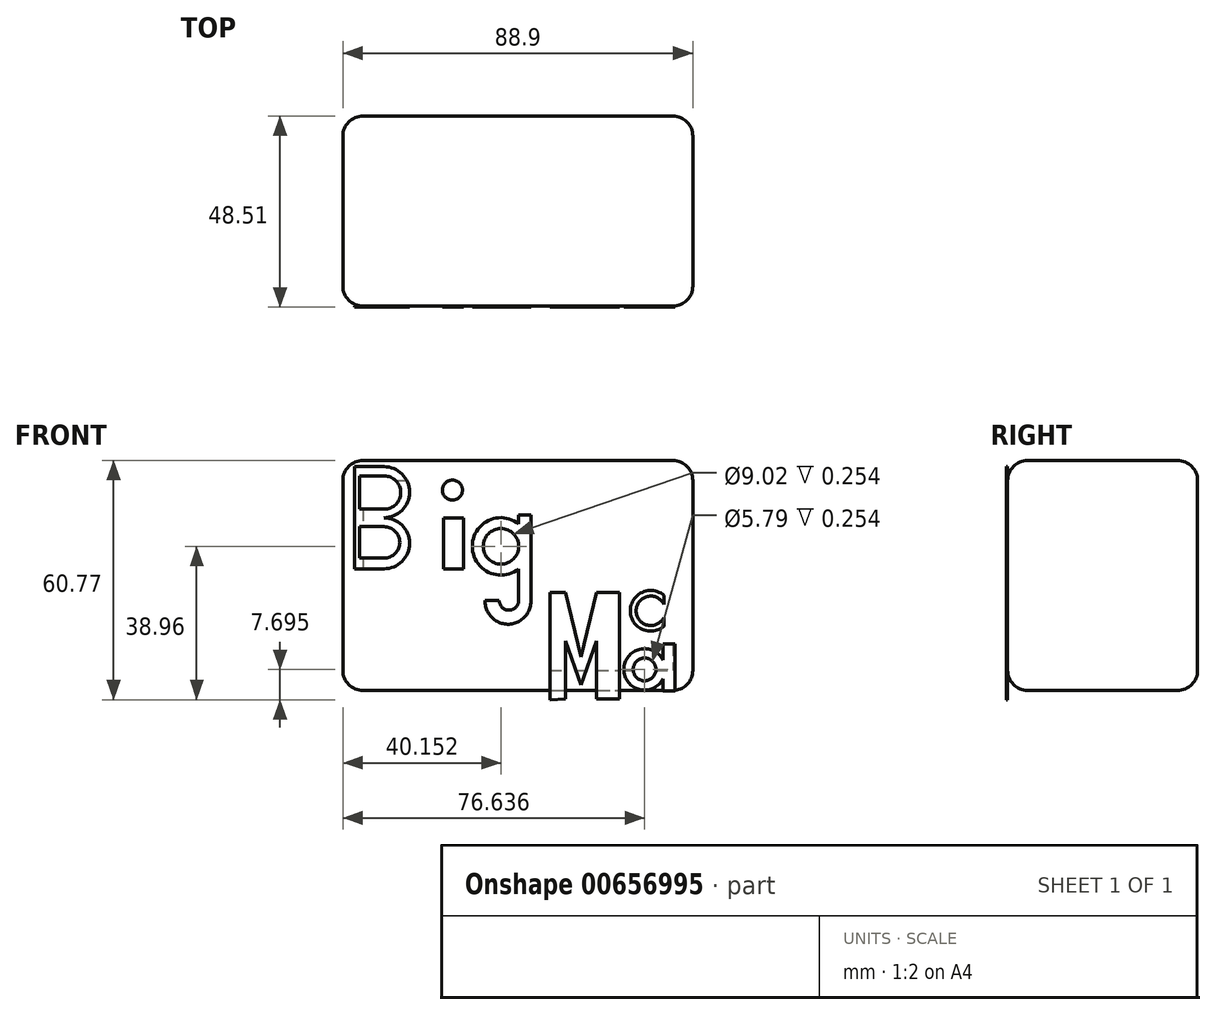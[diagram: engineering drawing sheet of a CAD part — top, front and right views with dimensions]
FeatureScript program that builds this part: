
annotation { "Feature Type Name" : "Feature", "Feature Type Description" : "" }
export const myFeature = defineFeature(function(context is Context, id is Id, definition is map)
    precondition{}
    {
        {
            var Q0;
            Q0=qCreatedBy(makeId("Front.planeOp"),FACE);
            var sketch = newSketch(context, id + "F0", { "sketchPlane" : qUnion([Q0])});
            skLineSegment(sketch, "E0.bottom", {"start": v(-44.67, 27.52) * mm, "end": v(44.23, 27.52) * mm});
            skLineSegment(sketch, "E0.top", {"start": v(-44.67, -30.9) * mm, "end": v(44.23, -30.9) * mm});
            skLineSegment(sketch, "E0.left", {"start": v(-44.67, 27.52) * mm, "end": v(-44.67, -30.9) * mm});
            skLineSegment(sketch, "E0.right", {"start": v(44.23, 27.52) * mm, "end": v(44.23, -30.9) * mm});
            skSolve(sketch);
        }
        {
            var Q0;
            Q0=makeQuery(id+"F0.imprint","IMPRINT",FACE,{"disambiguationData":[TD([[makeQuery(id+"F0.imprint","IMPRINT",EDGE,{"derivedFrom":sQuery(id+"F0.wireOp",EDGE,"E0.bottom")}),-1.0]])]});
            extrude(context, id + "F1", {"entities" : qUnion([Q0]), "depth" : 48.26 * mm, "offsetDistance" : 25.4 * mm});
        }
        {
            var Q0;
            Q0=makeQuery(id+"F1.opExtrude","CAP_EDGE",EDGE,{"disambiguationData":[OSD([sQuery(id+"F0.wireOp",EDGE,"E0.right")])],"isStart":false});
            var Q1;
            Q1=makeQuery(id+"F1.opExtrude","CAP_EDGE",EDGE,{"disambiguationData":[OSD([sQuery(id+"F0.wireOp",EDGE,"E0.top")])],"isStart":false});
            var Q2;
            Q2=makeQuery(id+"F1.opExtrude","SWEPT_EDGE",EDGE,{"disambiguationData":[OSD([sQuery(id+"F0.wireOp",EDGE,"E0.top"),sQuery(id+"F0.wireOp",EDGE,"E0.right")])]});
            var Q3;
            Q3=makeQuery(id+"F1.opExtrude","CAP_EDGE",EDGE,{"disambiguationData":[OSD([sQuery(id+"F0.wireOp",EDGE,"E0.right")])],"isStart":true});
            var Q4;
            Q4=makeQuery(id+"F1.opExtrude","SWEPT_EDGE",EDGE,{"disambiguationData":[OSD([sQuery(id+"F0.wireOp",EDGE,"E0.bottom"),sQuery(id+"F0.wireOp",EDGE,"E0.right")])]});
            var Q5;
            Q5=makeQuery(id+"F1.opExtrude","CAP_EDGE",EDGE,{"disambiguationData":[OSD([sQuery(id+"F0.wireOp",EDGE,"E0.bottom")])],"isStart":true});
            var Q6;
            Q6=makeQuery(id+"F1.opExtrude","CAP_EDGE",EDGE,{"disambiguationData":[OSD([sQuery(id+"F0.wireOp",EDGE,"E0.bottom")])],"isStart":false});
            var Q7;
            Q7=makeQuery(id+"F1.opExtrude","SWEPT_EDGE",EDGE,{"disambiguationData":[OSD([sQuery(id+"F0.wireOp",EDGE,"E0.bottom"),sQuery(id+"F0.wireOp",EDGE,"E0.left")])]});
            var Q8;
            Q8=makeQuery(id+"F1.opExtrude","SWEPT_EDGE",EDGE,{"disambiguationData":[OSD([sQuery(id+"F0.wireOp",EDGE,"E0.top"),sQuery(id+"F0.wireOp",EDGE,"E0.left")])]});
            var Q9;
            Q9=makeQuery(id+"F1.opExtrude","CAP_EDGE",EDGE,{"disambiguationData":[OSD([sQuery(id+"F0.wireOp",EDGE,"E0.left")])],"isStart":true});
            var Q10;
            Q10=makeQuery(id+"F1.opExtrude","CAP_EDGE",EDGE,{"disambiguationData":[OSD([sQuery(id+"F0.wireOp",EDGE,"E0.top")])],"isStart":true});
            var Q11;
            Q11=makeQuery(id+"F1.opExtrude","CAP_EDGE",EDGE,{"disambiguationData":[OSD([sQuery(id+"F0.wireOp",EDGE,"E0.left")])],"isStart":false});
            fillet(context, id + "F2", {"entities" : qUnion([Q0, Q1, Q2, Q3, Q4, Q5, Q6, Q7, Q8, Q9, Q10, Q11]), "radius" : 5.08 * mm, "tangentPropagation" : true, "allowEdgeOverflow" : false});
        }
        {
            var Q0;
            Q0=makeQuery(id+"F1.opExtrude","CAP_FACE",FACE,{"disambiguationData":[OSD([sQuery(id+"F0.wireOp",EDGE,"E0.bottom"),sQuery(id+"F0.wireOp",EDGE,"E0.top"),sQuery(id+"F0.wireOp",EDGE,"E0.left"),sQuery(id+"F0.wireOp",EDGE,"E0.right")])],"isStart":false});
            var sketch = newSketch(context, id + "F3", { "sketchPlane" : qUnion([Q0])});
            skLineSegment(sketch, "E1", {"start": v(-41.73, 25.97) * mm, "end": v(-41.73, 0) * mm});
            skLineSegment(sketch, "E2", {"start": v(-41.73, 0) * mm, "end": v(-34.25, 0) * mm});
            skLineSegment(sketch, "E3", {"start": v(-41.73, 25.97) * mm, "end": v(-34.25, 25.97) * mm});
            skArc(sketch, "E4", {"start": v(-34.25, 12.98) * mm, "mid": v(-27.76, 19.47) * mm, "end": v(-34.25, 25.97) * mm});
            skArc(sketch, "E5", {"start": v(-34.25, 0) * mm, "mid": v(-27.76, 6.5) * mm, "end": v(-34.25, 12.98) * mm});
            skLineSegment(sketch, "E6.0", {"start": v(-40.46, 23.6) * mm, "end": v(-40.46, 15.16) * mm});
            skLineSegment(sketch, "E7", {"start": v(-40.46, 23.6) * mm, "end": v(-34.2, 23.6) * mm});
            skLineSegment(sketch, "E8", {"start": v(-40.46, 15.16) * mm, "end": v(-34.2, 15.16) * mm});
            skArc(sketch, "E9", {"start": v(-34.2, 15.16) * mm, "mid": v(-29.98, 19.39) * mm, "end": v(-34.2, 23.6) * mm});
            skLineSegment(sketch, "E10.trimOffspring", {"start": v(-40.46, 10.72) * mm, "end": v(-40.46, 2.73) * mm});
            skPoint(sketch, "E11.orphan", {"position": v(-41.73, 12.98) * mm});
            skLineSegment(sketch, "E12", {"start": v(-40.46, 10.72) * mm, "end": v(-34.2, 10.72) * mm});
            skLineSegment(sketch, "E13", {"start": v(-40.46, 2.73) * mm, "end": v(-34.2, 2.73) * mm});
            skArc(sketch, "E14", {"start": v(-34.2, 2.73) * mm, "mid": v(-30.2, 6.72) * mm, "end": v(-34.2, 10.72) * mm});
            skLineSegment(sketch, "E15", {"start": v(-19.12, 12.98) * mm, "end": v(-19.12, 0) * mm});
            skLineSegment(sketch, "E16", {"start": v(-19.12, 0) * mm, "end": v(-14.04, 0) * mm});
            skLineSegment(sketch, "E17", {"start": v(-14.04, 0) * mm, "end": v(-14.04, 12.98) * mm});
            skLineSegment(sketch, "E18", {"start": v(-14.04, 12.98) * mm, "end": v(-19.12, 12.98) * mm});
            skCircle(sketch, "E19", {"center": v(-16.85, 20) * mm, "radius": 2.54 * mm});
            skLineSegment(sketch, "E20", {"start": v(0, 13.7) * mm, "end": v(0, 11.42) * mm});
            skLineSegment(sketch, "E21", {"start": v(0, 13.7) * mm, "end": v(3.1, 13.7) * mm});
            skLineSegment(sketch, "E22", {"start": v(3.1, 13.7) * mm, "end": v(3.1, -2.97) * mm});
            skLineSegment(sketch, "E23", {"start": v(0, 0) * mm, "end": v(0, -4.98) * mm});
            skLineSegment(sketch, "E24", {"start": v(3.1, -2.97) * mm, "end": v(3.1, -5.49) * mm});
            skArc(sketch, "E25", {"start": v(0, 11.42) * mm, "mid": v(-11.8, 5.71) * mm, "end": v(0, 0) * mm});
            skCircle(sketch, "E26", {"center": v(-4.52, 5.71) * mm, "radius": 4.5 * mm});
            skLineSegment(sketch, "E27", {"start": v(-4.98, -8.01) * mm, "end": v(-8.52, -8.01) * mm});
            skLineSegment(sketch, "E28", {"start": v(0, -4.98) * mm, "end": v(0, -8.01) * mm});
            skArc(sketch, "E29", {"start": v(-4.98, -8.01) * mm, "mid": v(-2.5, -10.5) * mm, "end": v(0, -8.01) * mm});
            skLineSegment(sketch, "E30", {"start": v(3.1, -5.49) * mm, "end": v(3.1, -8.27) * mm});
            skArc(sketch, "E31", {"start": v(-8.52, -8.01) * mm, "mid": v(-2.84, -14.07) * mm, "end": v(3.1, -8.27) * mm});
            skLineSegment(sketch, "E32", {"start": v(7.89, -33.25) * mm, "end": v(7.89, -6) * mm});
            skLineSegment(sketch, "E33", {"start": v(7.89, -6) * mm, "end": v(11.93, -6) * mm});
            skLineSegment(sketch, "E34", {"start": v(11.93, -6) * mm, "end": v(15.8, -22.39) * mm});
            skLineSegment(sketch, "E35", {"start": v(15.8, -22.39) * mm, "end": v(19.8, -6) * mm});
            skLineSegment(sketch, "E36", {"start": v(19.8, -6) * mm, "end": v(25.56, -6) * mm});
            skLineSegment(sketch, "E37", {"start": v(25.56, -6) * mm, "end": v(25.56, -33) * mm});
            skLineSegment(sketch, "E38", {"start": v(25.56, -33) * mm, "end": v(19.8, -33) * mm});
            skLineSegment(sketch, "E39", {"start": v(19.8, -33) * mm, "end": v(19.8, -18.36) * mm});
            skLineSegment(sketch, "E40", {"start": v(19.8, -18.36) * mm, "end": v(15.8, -29.47) * mm});
            skLineSegment(sketch, "E41", {"start": v(15.8, -29.47) * mm, "end": v(11.93, -18.36) * mm});
            skLineSegment(sketch, "E42", {"start": v(11.93, -18.36) * mm, "end": v(11.93, -33) * mm});
            skLineSegment(sketch, "E43", {"start": v(11.93, -33) * mm, "end": v(7.89, -33.25) * mm});
            skLineSegment(sketch, "E44", {"start": v(36.66, -23.16) * mm, "end": v(36.66, -19.12) * mm});
            skLineSegment(sketch, "E45", {"start": v(36.66, -19.12) * mm, "end": v(39.69, -19.12) * mm});
            skLineSegment(sketch, "E46", {"start": v(39.69, -19.12) * mm, "end": v(39.69, -30.98) * mm});
            skLineSegment(sketch, "E47", {"start": v(39.69, -30.98) * mm, "end": v(36.66, -30.98) * mm});
            skLineSegment(sketch, "E48", {"start": v(36.66, -30.98) * mm, "end": v(36.66, -27.95) * mm});
            skArc(sketch, "E49", {"start": v(36.66, -23.16) * mm, "mid": v(26.7, -25.56) * mm, "end": v(36.66, -27.95) * mm});
            skLineSegment(sketch, "E50", {"start": v(36.91, -6.75) * mm, "end": v(36.91, -9.02) * mm});
            skLineSegment(sketch, "E51", {"start": v(36.91, -12.3) * mm, "end": v(36.91, -14.58) * mm});
            skArc(sketch, "E52", {"start": v(36.91, -6.75) * mm, "mid": v(28.36, -10.66) * mm, "end": v(36.91, -14.58) * mm});
            skArc(sketch, "E53", {"start": v(36.91, -9.02) * mm, "mid": v(29.8, -10.66) * mm, "end": v(36.91, -12.3) * mm});
            skCircle(sketch, "E54", {"center": v(31.97, -25.56) * mm, "radius": 2.9 * mm});
            skSolve(sketch);
        }
        {
            var Q0;
            Q0 = qSketchRegion(id + "F3", true);
            extrude(context, id + "F4", {"entities" : qUnion([Q0]), "operationType" : NewBodyOperationType.ADD, "depth" : 0.25 * mm, "offsetDistance" : 25.4 * mm});
        }
    });
